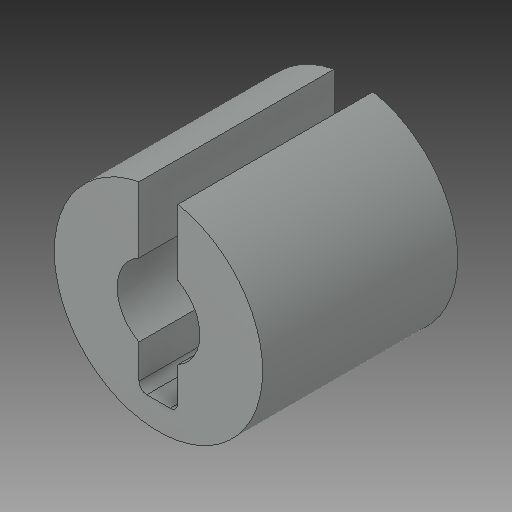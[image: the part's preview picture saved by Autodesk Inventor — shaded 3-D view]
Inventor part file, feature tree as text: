
AUTODESK INVENTOR PART (.ipt)
format: ipt  version: 2018 (Build 220112000, 112)  size: 112,640 bytes
history: native  units: in
note: dims shown in document units (in); Inventor stores cm internally (conversion verified against a paired STEP export)
features: fillet x1
ambient origin geometry x8: Origin, YZ Plane, XZ Plane, XY Plane, X Axis, Y Axis, Z Axis, Center Point
bodies: Solid1 (feature_tree)
feature tree (1):
  fillet  "Fillet1"  [1 undecoded]
note: 1 required parameter value undecoded (feature->parameter linkage not recoverable at this tier; creation-order binding heuristic only, values carry confidence <= 0.55)
